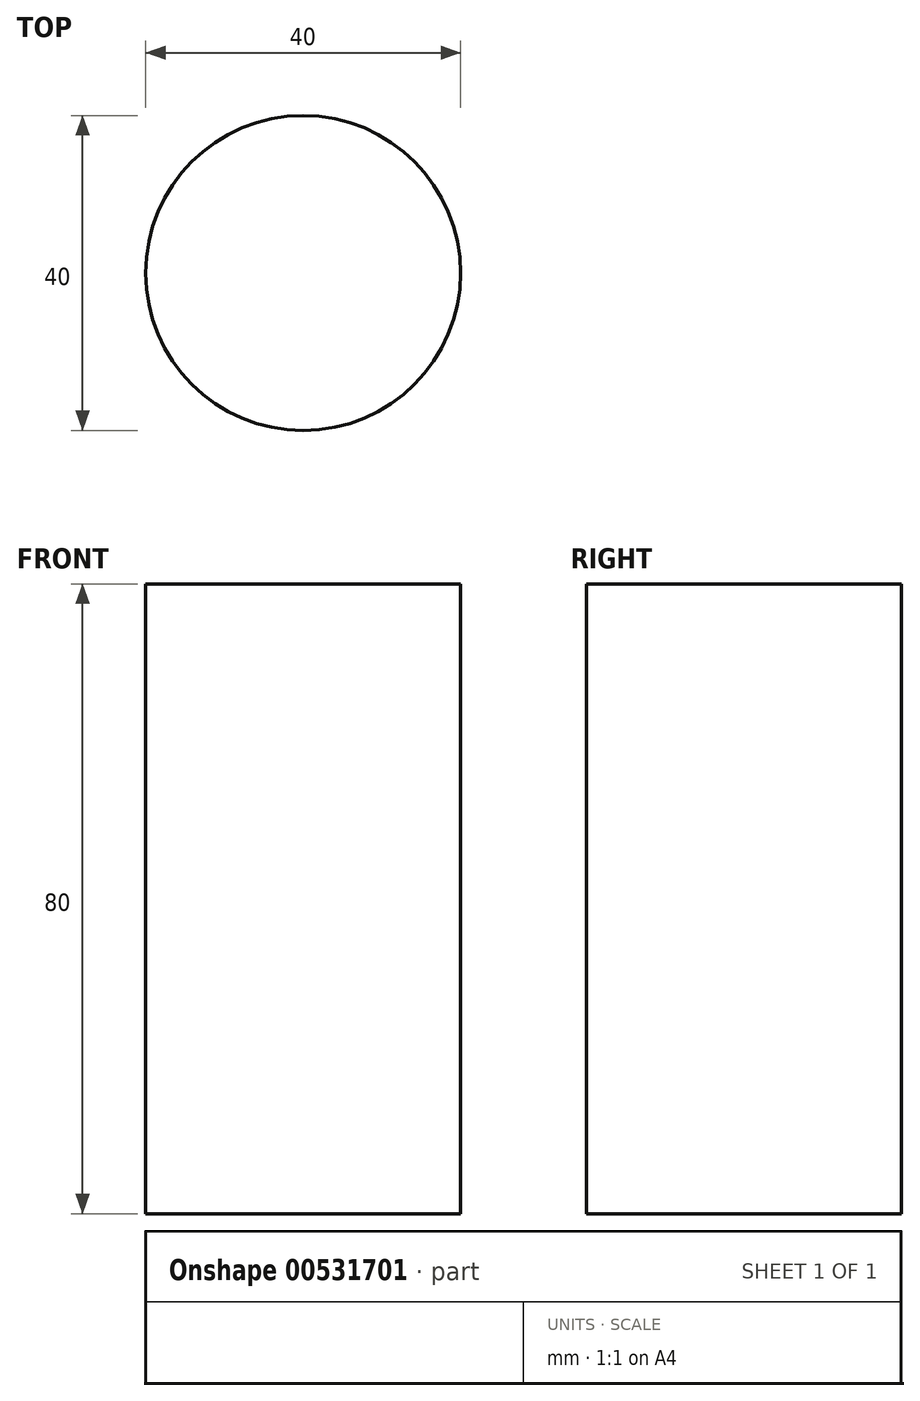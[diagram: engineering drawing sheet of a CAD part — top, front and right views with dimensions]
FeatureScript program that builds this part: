
annotation { "Feature Type Name" : "Feature", "Feature Type Description" : "" }
export const myFeature = defineFeature(function(context is Context, id is Id, definition is map)
    precondition{}
    {
        {
            var Q0;
            Q0=qCreatedBy(makeId("Top.planeOp"),FACE);
            var sketch = newSketch(context, id + "F0", { "sketchPlane" : qUnion([Q0])});
            skCircle(sketch, "E0", {"center": v(0, 0) * mm, "radius": 20 * mm});
            skSolve(sketch);
        }
        {
            var Q0;
            Q0 = qSketchRegion(id + "F0", true);
            extrude(context, id + "F1", {"entities" : qUnion([Q0]), "depth" : 80 * mm, "offsetDistance" : 25 * mm});
        }
    });
